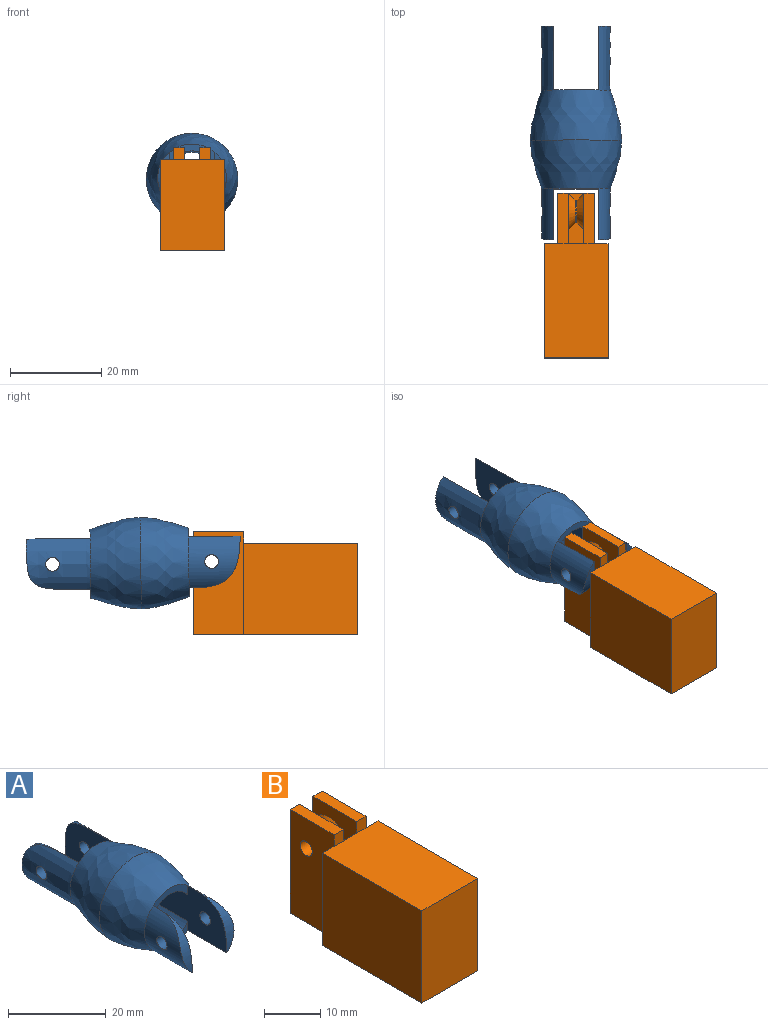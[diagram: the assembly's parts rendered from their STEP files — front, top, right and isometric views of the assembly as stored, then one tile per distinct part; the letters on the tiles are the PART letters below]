
ASSEMBLY  parts=2 mates=1
PART A: 22 faces, bbox 20x46.8x20 mm
  f0: plane 10x4.19mm, normal (0,-1,0), area 17mm2, adj f4,f6,f8,f21
  f1: plane 10x4.19mm, normal (0,-1,0), area 17mm2, adj f4,f6,f8,f20
  f2: plane 10.03x4.19mm, normal (0,1,0), area 17mm2, adj f5,f6,f8,f20
  f3: plane 10.03x4.19mm, normal (0,1,0), area 17mm2, adj f5,f6,f8,f21
  f4: bspline ~20x20mm, area 616.7mm2, adj f0,f1,f5,f14,f15
  f5: bspline ~20x20mm, area 644.4mm2, adj f2,f3,f4,f7,f9
  f6: plane 46.8x11.18mm, normal (-1,0,0), area 387.7mm2, adj f0,f1,f2,f3,f7,f12,f13,f14
  f7: extruded ~14x11.18mm, area 159.5mm2, adj f5,f6,f12,f13
  f8: plane 46.8x11.18mm, normal (1,0,0), area 387.7mm2, adj f0,f1,f2,f3,f9,f10,f11,f15
  f9: extruded ~14x11.18mm, area 159.5mm2, adj f5,f8,f10,f11
  f10: extruded ~14x11.18mm, area 22mm2, adj f8,f9
  f11: cylinder r=1.5mm len=3mm, axis (-1,0,0), area 22.1mm2, adj f8,f9
  f12: extruded ~14x11.18mm, area 22mm2, adj f6,f7
  f13: cylinder r=1.5mm len=3mm, axis (-1,0,0), area 22.1mm2, adj f6,f7
  f14: cylinder r=7.5mm len=11.3mm, axis (0,1,0), area 116.4mm2, adj f4,f6,f18,f19
  f15: cylinder r=7.5mm len=11.3mm, axis (0,1,0), area 116.4mm2, adj f4,f8,f16,f17
  f16: extruded ~11.3x11.18mm, area 22.9mm2, adj f8,f15
  f17: cylinder r=1.5mm len=3mm, axis (-1,0,0), area 22.3mm2, adj f8,f15
  f18: extruded ~11.3x11.18mm, area 22.9mm2, adj f6,f14
  f19: cylinder r=1.5mm len=3mm, axis (-1,0,0), area 22.3mm2, adj f6,f14
  f20: cylinder r=6mm len=21.5mm, axis (0,1,0), area 254.2mm2, adj f1,f2,f6,f8
  f21: cylinder r=6mm len=21.5mm, axis (0,1,0), area 254.2mm2, adj f0,f3,f6,f8
PART B: 22 faces, bbox 14x36x22.5 mm
  f0: plane 2.5x2.3mm, normal (0,-1,0), area 5.7mm2, adj f3,f4,f5,f13
  f1: plane 2.5x2.3mm, normal (0,-1,0), area 5.7mm2, adj f8,f9,f10,f13
  f2: plane 11x3.4mm, normal (0,0,1), area 37.4mm2, adj f3,f7,f8,f12
  f3: plane 12.7x11mm, normal (1,0,0), area 89.4mm2, adj f0,f2,f4,f7,f12,f20
  f4: plane 11x2.3mm, normal (0,0,1), area 25.3mm2, adj f0,f3,f5,f7
  f5: plane 22.5x11mm, normal (-1,0,0), area 240.4mm2, adj f0,f4,f6,f7,f17,f18
  f6: plane 36x14mm, normal (0,0,-1), area 438mm2, adj f5,f7,f10,f11,f14,f15,f16,f17
  f7: plane 22.5x8mm, normal (0,1,0), area 136.8mm2, adj f2,f3,f4,f5,f6,f8,f9,f10
  f8: plane 12.7x11mm, normal (-1,0,0), area 89.4mm2, adj f1,f2,f7,f9,f12,f21
  f9: plane 11x2.3mm, normal (0,0,1), area 25.3mm2, adj f1,f7,f8,f10
  f10: plane 22.5x11mm, normal (1,0,0), area 240.4mm2, adj f1,f6,f7,f9,f11,f18
  f11: plane 20x3mm, normal (0,1,0), area 60mm2, adj f6,f10,f13,f15
  f12: plane 10.2x3.4mm, normal (0,1,0), area 34.7mm2, adj f2,f3,f8,f13
  f13: plane 25x14mm, normal (0,0,1), area 350mm2, adj f0,f1,f11,f12,f14,f15,f16,f17
  f14: plane 25x20mm, normal (-1,0,0), area 500mm2, adj f6,f13,f16,f17
  f15: plane 25x20mm, normal (1,0,0), area 500mm2, adj f6,f11,f13,f16
  f16: plane 20x14mm, normal (0,-1,0), area 280mm2, adj f6,f13,f14,f15
  f17: plane 20x3mm, normal (0,1,0), area 60mm2, adj f5,f6,f13,f14
  f18: cylinder r=1.5mm len=8mm, axis (1,0,0), area 75.4mm2, adj f5,f10
  f19: cylinder r=2.5mm len=5mm, axis (1,0,0), area 6.3mm2, adj f20,f21
  f20: cone r=2.5mm half-angle=45deg, axis (-1,0,0), area 43.3mm2, adj f3,f19
  f21: cone r=2.5mm half-angle=45deg, axis (1,0,0), area 43.3mm2, adj f8,f19
PLACE A rot(axis=(0,1,-0.01),180deg) t=(-20.6,7.04,21.74)mm
PLACE B t=(-20.6,6.81,-10.2)mm fixed
MATE revolute A.f17 <-> B.f18  axis (1,0,0) through (-25.6,2.81,5.8)mm
